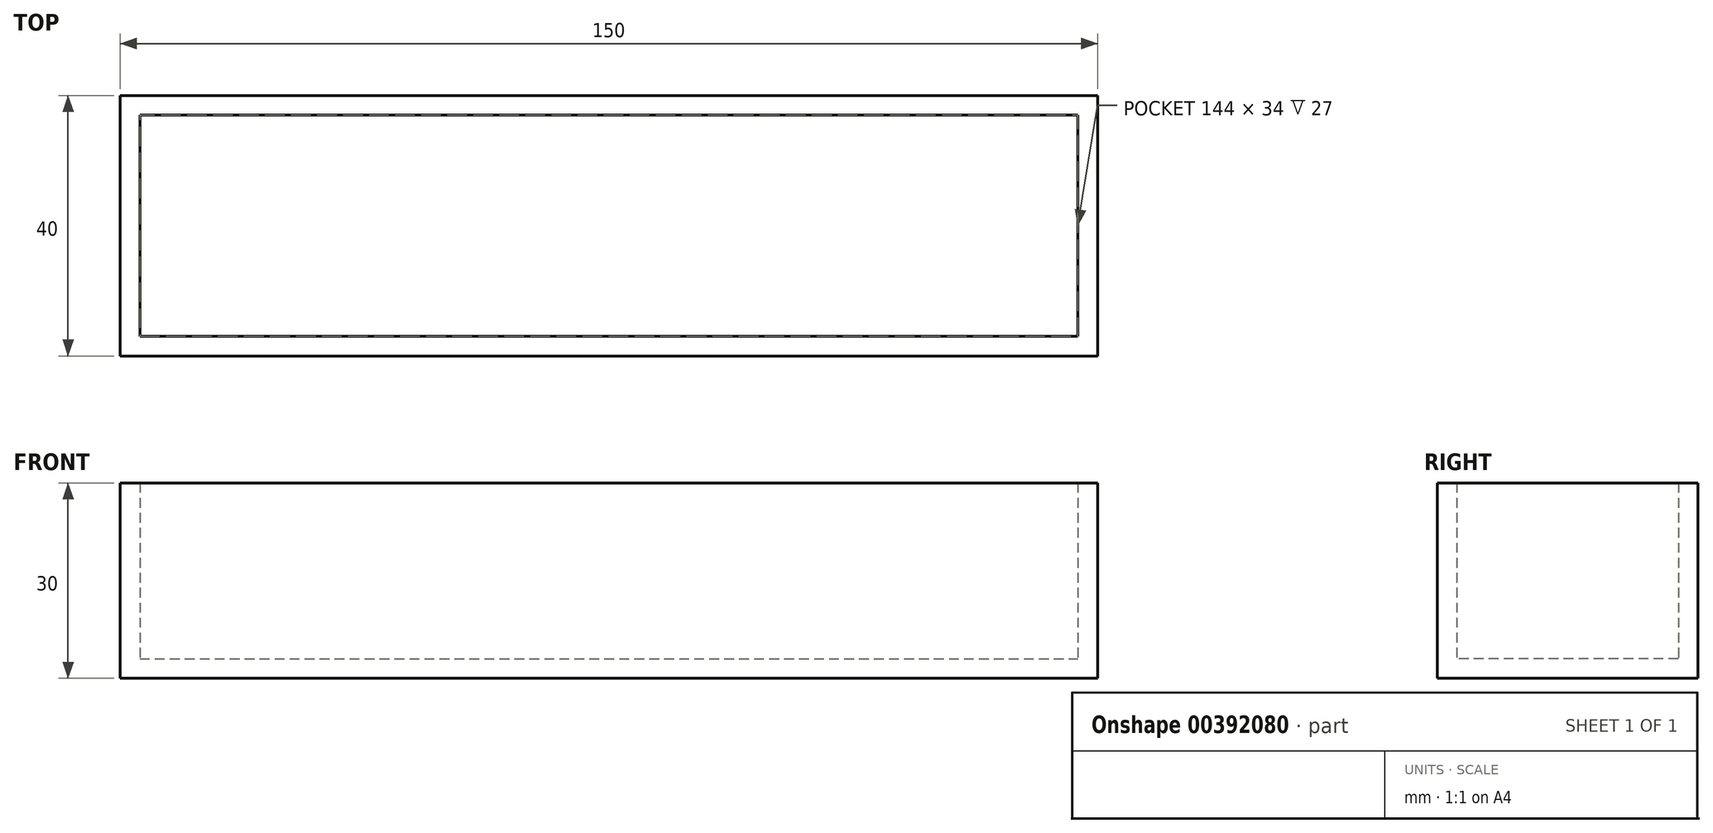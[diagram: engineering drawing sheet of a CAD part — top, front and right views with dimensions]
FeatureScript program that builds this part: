
annotation { "Feature Type Name" : "Feature", "Feature Type Description" : "" }
export const myFeature = defineFeature(function(context is Context, id is Id, definition is map)
    precondition{}
    {
        {
            var Q0;
            Q0=qCreatedBy(makeId("Top.planeOp"),FACE);
            var sketch = newSketch(context, id + "F0", { "sketchPlane" : qUnion([Q0])});
            skLineSegment(sketch, "E0.bottom", {"start": v(-75, 20) * mm, "end": v(75, 20) * mm});
            skLineSegment(sketch, "E0.top", {"start": v(-75, -20) * mm, "end": v(75, -20) * mm});
            skLineSegment(sketch, "E0.left", {"start": v(-75, 20) * mm, "end": v(-75, -20) * mm});
            skLineSegment(sketch, "E0.right", {"start": v(75, 20) * mm, "end": v(75, -20) * mm});
            skLineSegment(sketch, "E1", {"start": v(-75, 20) * mm, "end": v(75, -20) * mm, "construction": true});
            skSolve(sketch);
        }
        {
            var Q0;
            Q0 = qSketchRegion(id + "F0", true);
            extrude(context, id + "F1", {"entities" : qUnion([Q0]), "depth" : 30 * mm});
        }
        {
            var Q0;
            Q0=qCreatedBy(makeId("Top.planeOp"),FACE);
            cPlane(context, id + "F2", {"entities" : qUnion([Q0]), "cplaneType" : CPlaneType.OFFSET, "offset" : 3 * mm, "width" : 150 * mm, "height" : 150 * mm});
        }
        {
            var Q0;
            Q0=qCreatedBy(id+"F2.planeOp",FACE);
            var sketch = newSketch(context, id + "F3", { "sketchPlane" : qUnion([Q0])});
            skLineSegment(sketch, "E2.bottom", {"start": v(-72, 17) * mm, "end": v(72, 17) * mm});
            skLineSegment(sketch, "E2.top", {"start": v(-72, -17) * mm, "end": v(72, -17) * mm});
            skLineSegment(sketch, "E2.left", {"start": v(-72, 17) * mm, "end": v(-72, -17) * mm});
            skLineSegment(sketch, "E2.right", {"start": v(72, 17) * mm, "end": v(72, -17) * mm});
            skLineSegment(sketch, "E3", {"start": v(-72, 17) * mm, "end": v(72, -17) * mm, "construction": true});
            skSolve(sketch);
        }
        {
            var Q0;
            Q0 = qSketchRegion(id + "F3", true);
            extrude(context, id + "F4", {"entities" : qUnion([Q0]), "operationType" : NewBodyOperationType.REMOVE, "depth" : 27 * mm});
        }
    });
